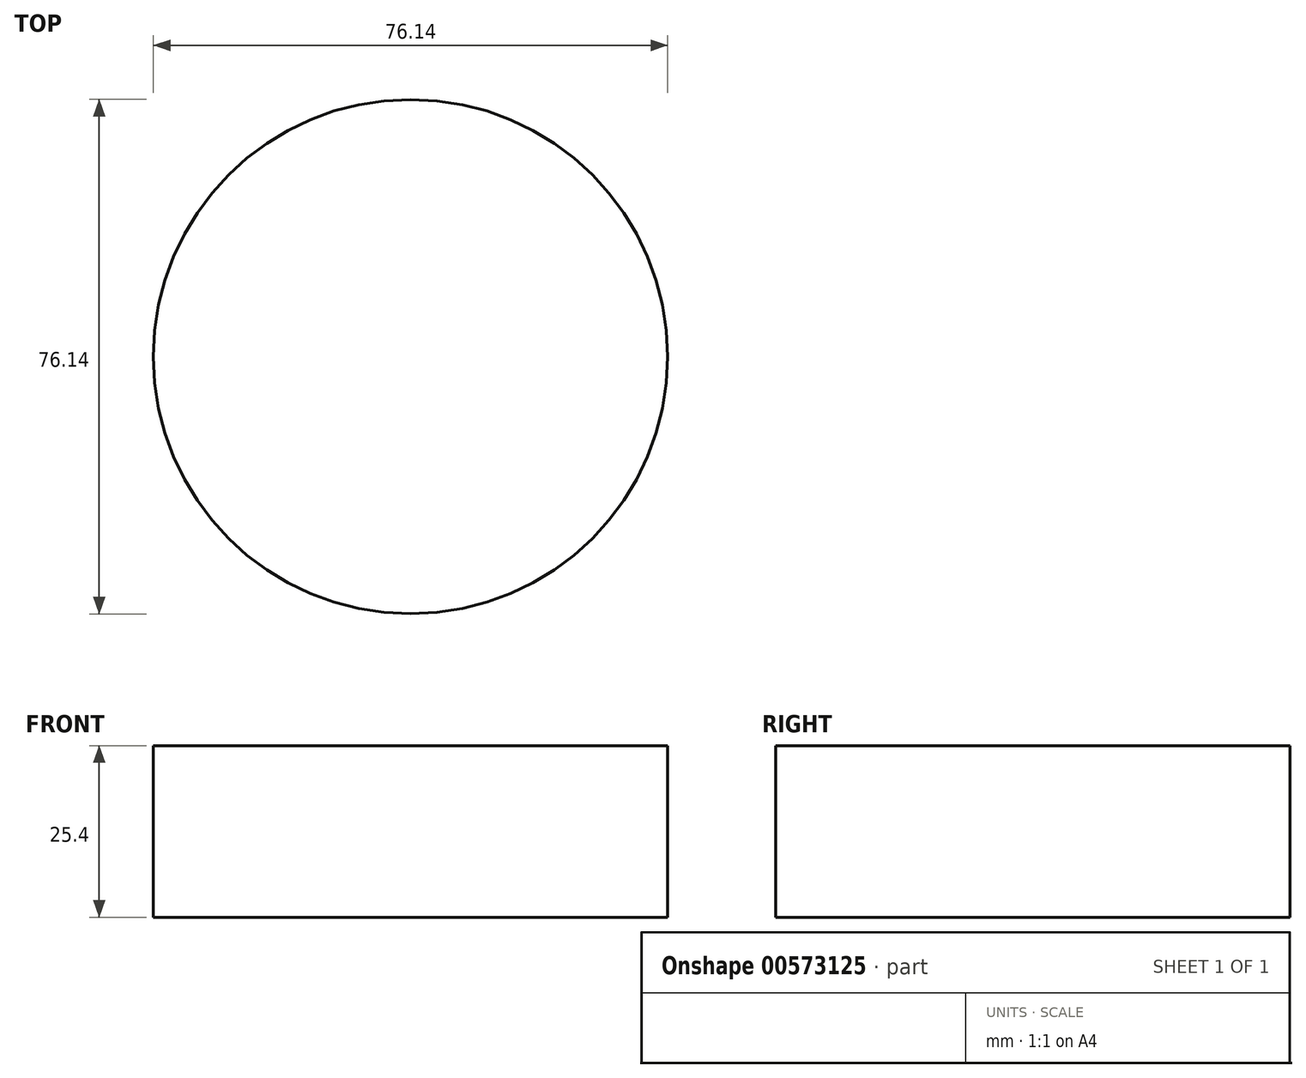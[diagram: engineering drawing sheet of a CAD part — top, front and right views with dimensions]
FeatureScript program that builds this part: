
annotation { "Feature Type Name" : "Feature", "Feature Type Description" : "" }
export const myFeature = defineFeature(function(context is Context, id is Id, definition is map)
    precondition{}
    {
        {
            var Q0;
            Q0=qCreatedBy(makeId("Top.planeOp"),FACE);
            var sketch = newSketch(context, id + "F0", { "sketchPlane" : qUnion([Q0])});
            skCircle(sketch, "E0", {"center": v(0, 0) * mm, "radius": 38.07 * mm});
            skSolve(sketch);
        }
        {
            var Q0;
            Q0 = qSketchRegion(id + "F0", true);
            extrude(context, id + "F1", {"entities" : qUnion([Q0]), "depth" : 25.4 * mm, "offsetDistance" : 25.4 * mm});
        }
    });
